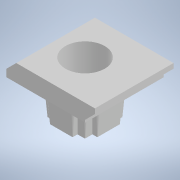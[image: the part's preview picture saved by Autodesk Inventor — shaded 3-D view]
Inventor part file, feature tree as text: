
AUTODESK INVENTOR PART (.ipt)
format: ipt  version: 2021 (Build 250183000, 183)  size: 183,808 bytes
history: native  units: mm
features: other x21, sketch x3, extrude x2, hole x1
ambient origin geometry x8: Origin, YZ Plane, XZ Plane, XY Plane, X Axis, Y Axis, Z Axis, Center Point
bodies: Solid1 (feature_tree)
feature tree (27):
  extrude  "Extrusion1"  Depth=32.0mm
  extrude  "Extrusion2"  TaperAngle=0.0deg  [1 undecoded]
  hole  "Hole1"  [1 undecoded]
  other  "insrt_to_lock_XY"
  other  "insrt_to_lock_YZ"
  other  "insrt_to_lock_ZX"
  other  "insrt_to_lock_X"
  other  "insrt_to_lock_Y"
  other  "insrt_to_lock_Z"
  other  "insrt_to_lock_Center"
  other  "lock_to_body_XY"
  other  "lock_to_body_YZ"
  other  "lock_to_body_ZX"
  other  "lock_to_body_X"
  other  "lock_to_body_Y"
  other  "lock_to_body_Z"
  other  "lock_to_body_Center"
  other  "washer_XY"
  other  "washer_YZ"
  other  "washer_ZX"
  other  "washer_X"
  other  "washer_Y"
  other  "washer_Z"
  other  "washer_Center"
  sketch  "Sketch_1"  dims[d0=32.0mm d1=0.0mm d2=15.0mm d3=-0.872665mm]
  sketch  "Sketch_2"  dims[d4=10.2mm d5=6.0mm d6=16.0mm d7=18.5mm d8=90.0deg d9=21.0mm d10=0.0mm d11=0.0mm d12=0.0mm]
  sketch  "Sketch3"
note: 2 required parameter values undecoded (feature->parameter linkage not recoverable at this tier; creation-order binding heuristic only, values carry confidence <= 0.55)
